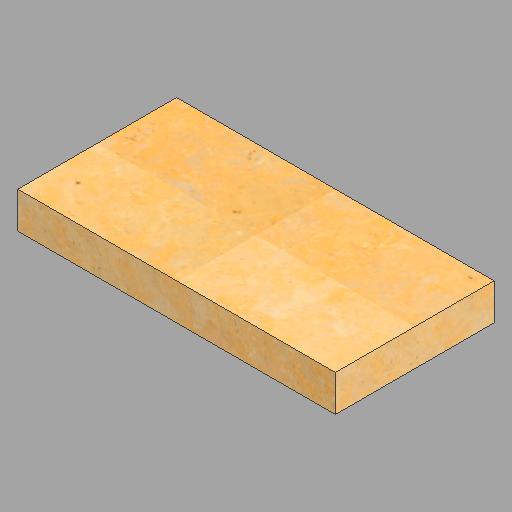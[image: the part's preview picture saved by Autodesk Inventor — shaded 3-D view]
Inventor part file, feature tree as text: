
AUTODESK INVENTOR PART (.ipt)
format: ipt  version: 2023 (Build 270158030, 158C)  size: 427,520 bytes
history: native  units: in
note: dims shown in document units (in); Inventor stores cm internally (conversion verified against a paired STEP export)
features: extrude x1, sketch x1
ambient origin geometry x8: Origin, YZ Plane, XZ Plane, XY Plane, X Axis, Y Axis, Z Axis, Center Point
bodies: Solid1 (feature_tree)
feature tree (2):
  extrude  "Extrusion1"  Depth=12.0in
  sketch  "Sketch1"  dims[d0=24.0in d1=12.0in d2=2.75in d3=0.0in]
